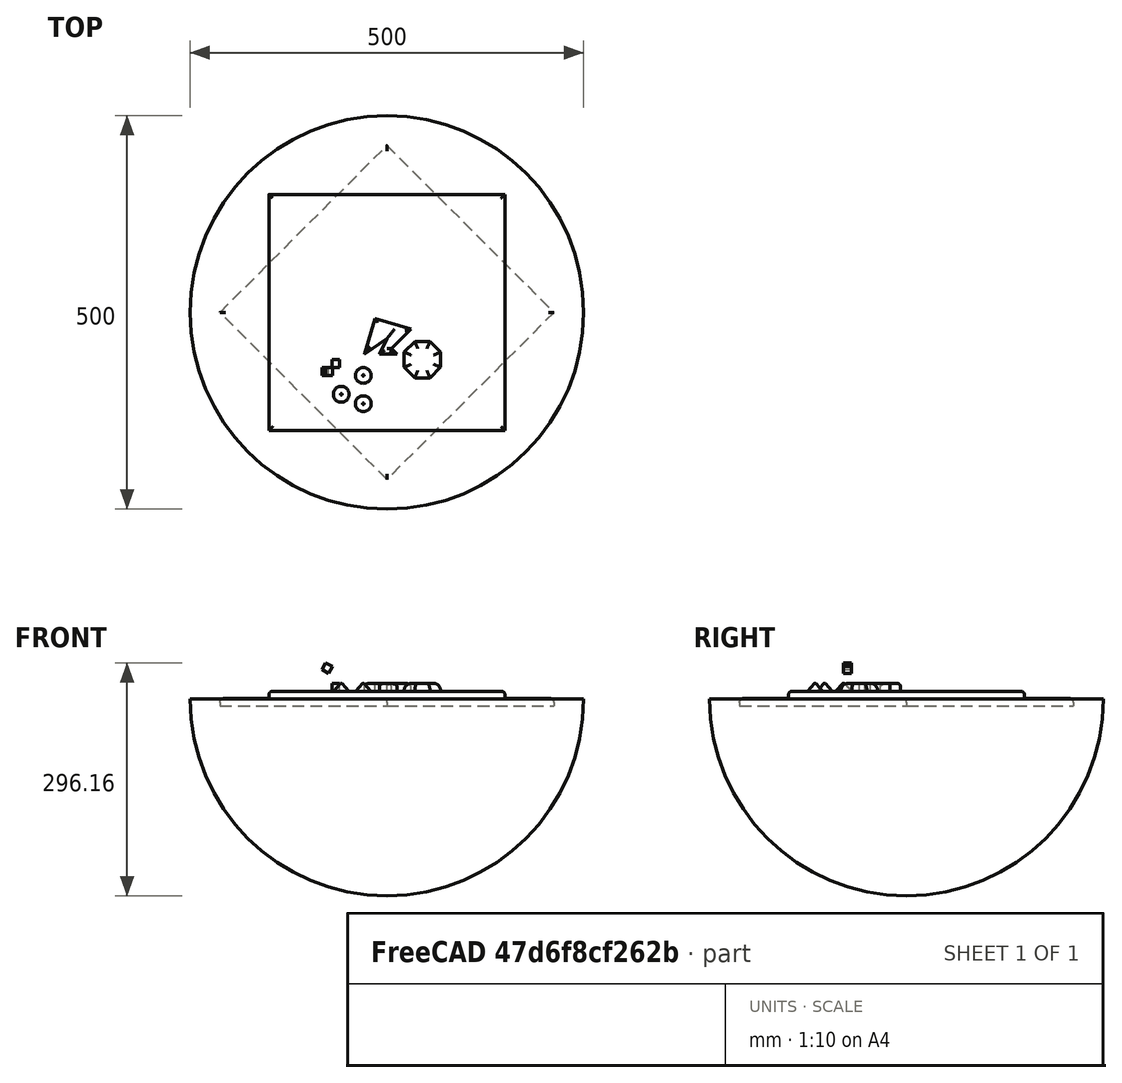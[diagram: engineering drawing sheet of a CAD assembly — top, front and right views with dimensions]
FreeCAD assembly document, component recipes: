
FREECAD ASSEMBLY — COMPONENT RECIPES ("assembly__export")

This assembly document has 7 components, labeled P0..P6 below (a component is one placed body or linked part). 5 of them carry a construction recipe — the FreeCAD feature program that regenerates the part from scratch, quoted from this document or its linked companion documents; the rest are supplied as boundary geometry only. No exploded tour is included for this assembly.
COMPONENT P0 — recipe-attached ("root_body", modeled in this document).
Construction recipe (the document's own serialized feature program — sketch geometry with constraints, then the solid features built on it; lengths are millimeters unless a unit is written):

FEATURE [Sketcher::SketchObject] Sketch002
  MapMode = 5
  Support = -> [XY_Plane005]
  sketch-geometry (7):
    g0: LineSegment StartX=-15.1232 StartY=25.4281 StartZ=0 EndX=-28.6703 EndY=-20.0752 EndZ=0
    g1: LineSegment StartX=-28.6703 StartY=-20.0752 StartZ=0 EndX=-3.6e-15 EndY=0 EndZ=0
    g2: LineSegment StartX=-3.6e-15 StartY=0 StartZ=0 EndX=-9.2976 EndY=-19.9388 EndZ=0
    g3: LineSegment StartX=-9.2976 StartY=-19.9388 StartZ=0 EndX=12.7024 EndY=-19.9388 EndZ=0
    g4: LineSegment StartX=12.7024 StartY=-19.9388 StartZ=0 EndX=5.63133 EndY=-12.8677 EndZ=0
    g5: LineSegment StartX=5.63133 StartY=-12.8677 StartZ=0 EndX=30.3801 EndY=11.881 EndZ=0
    g6: LineSegment StartX=30.3801 StartY=11.881 StartZ=0 EndX=-15.1232 EndY=25.4281 EndZ=0
  constraints (20):
    c: Coincident(g0,g1)
    c: Coincident(g1,g2)
    c: Coincident(g2,g3)
    c: Coincident(g3,g4)
    c: Coincident(g4,g5)
    c: Coincident(g5,g6)
    c: Coincident(g6,g0)
    c: Coincident(g1,g-1)
    c: Perpendicular(g5,g4)
    c: Perpendicular(g6,g0)
    c: Equal(g0,g6)
    c: Equal(g2,g3)
    c: Equal(g1,g5)
    c: Angle(g1,g2) = 0.523599
    c: Angle(g4,g3) = 0.785398
    c: Horizontal(g3)
    c: Distance(g4) = 10
    c: Distance(g1) = 35
    c: Angle(g3,g2) = 1.13446
    c: Distance(g2) = 22
FEATURE [PartDesign::Pad] Pad002
  Length = 10
  Length2 = 100
  Profile = -> Sketch002
  Type = 0
FEATURE [PartDesign::Fillet] Fillet002
  Base = -> Pad002 [Face9]
  BaseFeature = -> Pad002
  Radius = 4
FEATURE [PartDesign::Body] Body002  label="root_body"
  Group = -> [Sketch002,Pad002,Fillet002]
  Origin = -> Origin005
  Placement = pos=(0,-33,0) rot=(0,0,1;0rad)
  Tip = -> Fillet002
COMPONENT P1 — recipe-attached ("cube_part_clone_Body", modeled in this document).
Construction recipe (the document's own serialized feature program — sketch geometry with constraints, then the solid features built on it; lengths are millimeters unless a unit is written):

FEATURE [PartDesign::FeatureBase] Clone  label="cube_part_clone"
  BaseFeature = -> Box001
  Placement = pos=(-55,-57,0) rot=(0,0,1;0rad)
FEATURE [PartDesign::Body] Body003  label="cube_part_clone_Body"
  BaseFeature = -> Box001
  Group = -> [Clone]
  Origin = -> Origin006
  Placement = pos=(-35,-23,0) rot=(0,1,0;0.523599rad)
  Tip = -> Clone
COMPONENT P2 — recipe-attached ("floor_body_clone_Body", modeled in this document).
Construction recipe (the document's own serialized feature program — sketch geometry with constraints, then the solid features built on it; lengths are millimeters unless a unit is written):

FEATURE [PartDesign::FeatureBase] Clone001  label="floor_body_clone"
  BaseFeature = -> Body
FEATURE [PartDesign::Body] Body004  label="floor_body_clone_Body"
  BaseFeature = -> Body
  Group = -> [Clone001]
  Origin = -> Origin007
  Placement = pos=(0,0,-9) rot=(0,0,1;0.785398rad)
  Tip = -> Clone001
COMPONENT P3 — geometry summary ("my_final_assembly"; no construction recipe available for this part):
  bounding box: 160.0 x 150.0 x 21.0 mm
  tessellated surface: 131,360 triangles
  volume: 247423 mm^3 (49% of its bounding box)
COMPONENT P4 — recipe-attached ("octagon_part", modeled in this document).
Construction recipe (the document's own serialized feature program — sketch geometry with constraints, then the solid features built on it; lengths are millimeters unless a unit is written):

FEATURE [Sketcher::SketchObject] Sketch001  label="octagon_sketch"
  MapMode = 5
  Support = -> [XY_Plane003]
  sketch-geometry (9):
    g0: LineSegment StartX=23.097 StartY=-9.56709 StartZ=0 EndX=23.097 EndY=9.56709 EndZ=0
    g1: LineSegment StartX=23.097 StartY=9.56709 StartZ=0 EndX=9.56709 EndY=23.097 EndZ=0
    g2: LineSegment StartX=9.56709 StartY=23.097 StartZ=0 EndX=-9.56709 EndY=23.097 EndZ=0
    g3: LineSegment StartX=-9.56709 StartY=23.097 StartZ=0 EndX=-23.097 EndY=9.56709 EndZ=0
    g4: LineSegment StartX=-23.097 StartY=9.56709 StartZ=0 EndX=-23.097 EndY=-9.56709 EndZ=0
    g5: LineSegment StartX=-23.097 StartY=-9.56709 StartZ=0 EndX=-9.56709 EndY=-23.097 EndZ=0
    g6: LineSegment StartX=-9.56709 StartY=-23.097 StartZ=0 EndX=9.56709 EndY=-23.097 EndZ=0
    g7: LineSegment StartX=9.56709 StartY=-23.097 StartZ=0 EndX=23.097 EndY=-9.56709 EndZ=0
    g8: Circle [constr] CenterX=0 CenterY=0 CenterZ=0 NormalX=0 NormalY=0 NormalZ=1 AngleXU=0 Radius=25
  constraints (20):
    c: Coincident(g0,g1)
    c: Coincident(g1,g2)
    c: Coincident(g2,g3)
    c: Coincident(g3,g4)
    c: Coincident(g4,g5)
    c: Coincident(g5,g6)
    c: Coincident(g6,g7)
    c: Coincident(g7,g0)
    c: Equal(g0, g1-g7) x7
    c: PointOnObject(g0,g8)
    c: PointOnObject(g1,g8)
    c: PointOnObject(g2,g8)
    c: PointOnObject(g3,g8)
    c: PointOnObject(g4,g8)
    c: PointOnObject(g5,g8)
    c: PointOnObject(g6,g8)
    c: PointOnObject(g7,g8)
    c: Coincident(g8,g-1)
    c: Horizontal(g6)
    c: Radius(g8) = 25
FEATURE [PartDesign::Pad] Pad001  label="octagon_Pad"
  Length = 10
  Length2 = 100
  Profile = -> Sketch001
  Type = 0
FEATURE [PartDesign::Fillet] Fillet  label="octagon_Fillet"
  Base = -> Pad001 [Face10]
  BaseFeature = -> Pad001
  Radius = 9
FEATURE [PartDesign::Body] Body001  label="octagon_body"
  Group = -> [Sketch001,Pad001,Fillet]
  Origin = -> Origin003
  Placement = pos=(45,-60,0) rot=(0,0,1;0rad)
  Tip = -> Fillet
COMPONENT P5 — recipe-attached ("floor_part", modeled in this document).
Construction recipe (the document's own serialized feature program — sketch geometry with constraints, then the solid features built on it; lengths are millimeters unless a unit is written):

FEATURE [Sketcher::SketchObject] Sketch  label="floor_Sketch"
  MapMode = 5
  Support = -> [XY_Plane001]
  sketch-geometry (4):
    g0: LineSegment StartX=-150 StartY=150 StartZ=0 EndX=150 EndY=150 EndZ=0
    g1: LineSegment StartX=150 StartY=150 StartZ=0 EndX=150 EndY=-150 EndZ=0
    g2: LineSegment StartX=150 StartY=-150 StartZ=0 EndX=-150 EndY=-150 EndZ=0
    g3: LineSegment StartX=-150 StartY=-150 StartZ=0 EndX=-150 EndY=150 EndZ=0
  constraints (11):
    c: Coincident(g0,g1)
    c: Coincident(g1,g2)
    c: Coincident(g2,g3)
    c: Coincident(g3,g0)
    c: Horizontal(g0)
    c: Horizontal(g2)
    c: Vertical(g1)
    c: Vertical(g3)
    c: Symmetric(g0,g1,g-1)
    c: Equal(g0,g3)
    c: DistanceX(g2,g2) = 300
FEATURE [PartDesign::Pad] Pad  label="floor_Pad"
  Length = 10
  Length2 = 100
  Profile = -> Sketch
  Reversed = true
  Type = 0
FEATURE [PartDesign::Fillet] Fillet001
  Base = -> Pad [Face5]
  BaseFeature = -> Pad
  Radius = 5
FEATURE [PartDesign::Body] Body  label="floor_body"
  Group = -> [Sketch,Pad,Fillet001]
  Origin = -> Origin001
  Tip = -> Fillet001
COMPONENT P6 — geometry summary ("deco_Part"; no construction recipe available for this part):
  bounding box: 79.0 x 48.0 x 10.0 mm
  tessellated surface: 3,210 triangles
  volume: 4487 mm^3 (12% of its bounding box)
PROVENANCE & LICENSES
A FreeCAD (.FCStd) document from a public repository crawl; recipes are the document's own serialized feature recipes (and, for linked parts, companion documents' recipes).
License: mit.
